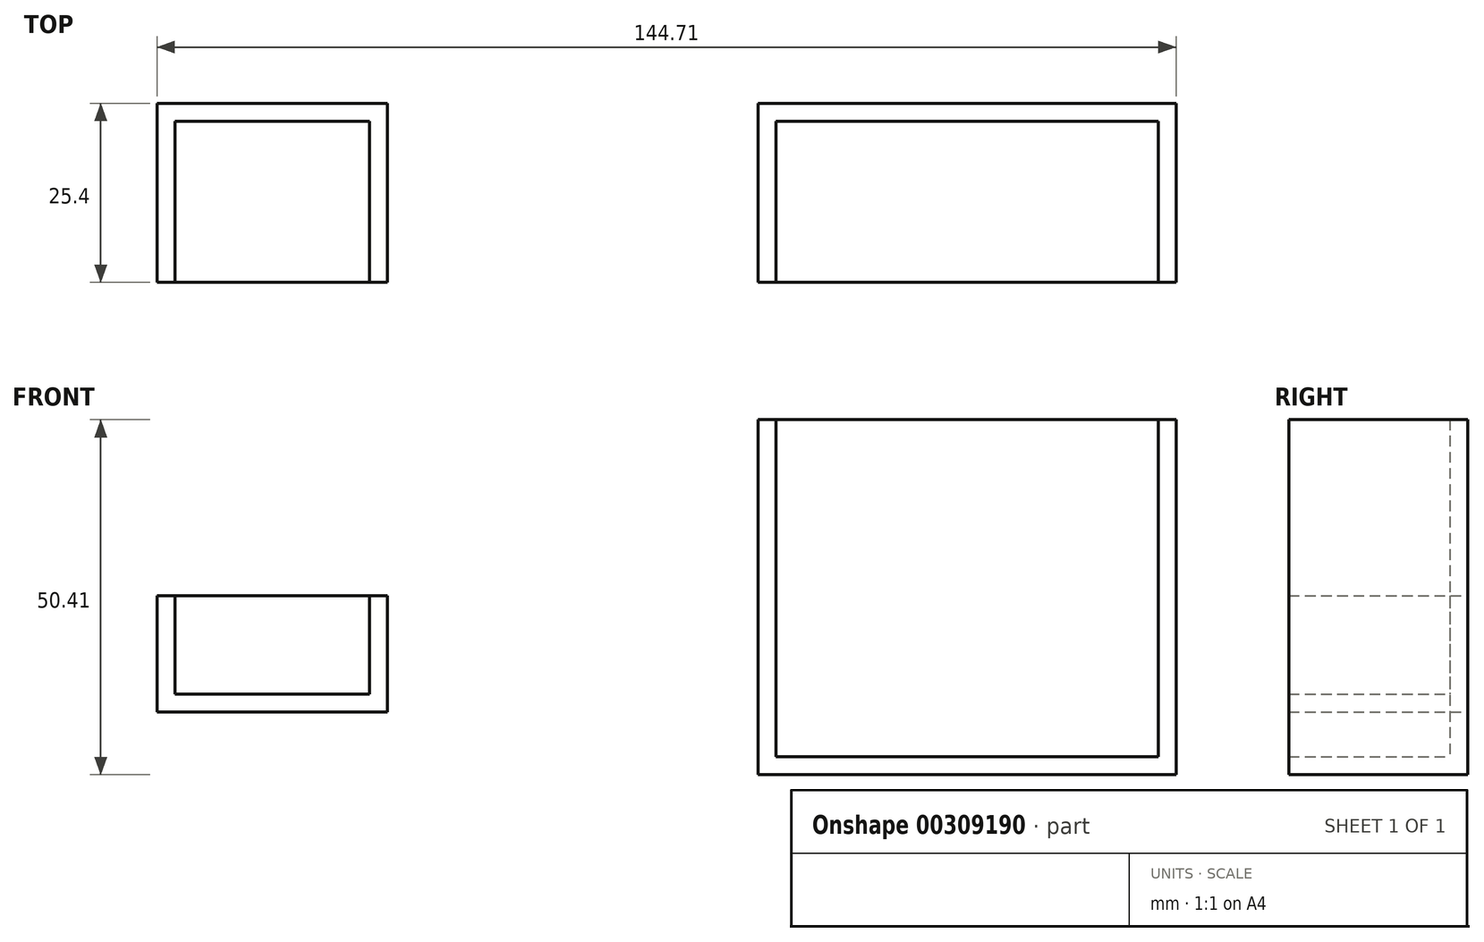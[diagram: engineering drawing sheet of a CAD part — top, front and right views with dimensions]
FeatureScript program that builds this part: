
annotation { "Feature Type Name" : "Feature", "Feature Type Description" : "" }
export const myFeature = defineFeature(function(context is Context, id is Id, definition is map)
    precondition{}
    {
        {
            var Q0;
            Q0=qCreatedBy(makeId("Front.planeOp"),FACE);
            var sketch = newSketch(context, id + "F0", { "sketchPlane" : qUnion([Q0])});
            skLineSegment(sketch, "E0.bottom", {"start": v(-111.29, 57.65) * mm, "end": v(-78.58, 57.65) * mm});
            skLineSegment(sketch, "E0.top", {"start": v(-111.29, 41.14) * mm, "end": v(-78.58, 41.14) * mm});
            skLineSegment(sketch, "E0.left", {"start": v(-111.29, 57.65) * mm, "end": v(-111.29, 41.14) * mm});
            skLineSegment(sketch, "E0.right", {"start": v(-78.58, 57.65) * mm, "end": v(-78.58, 41.14) * mm});
            skLineSegment(sketch, "E1.bottom", {"start": v(-25.96, 82.64) * mm, "end": v(33.42, 82.64) * mm});
            skLineSegment(sketch, "E1.top", {"start": v(-25.96, 32.23) * mm, "end": v(33.42, 32.23) * mm});
            skLineSegment(sketch, "E1.left", {"start": v(-25.96, 82.64) * mm, "end": v(-25.96, 32.23) * mm});
            skLineSegment(sketch, "E1.right", {"start": v(33.42, 82.64) * mm, "end": v(33.42, 32.23) * mm});
            skSolve(sketch);
        }
        {
            var Q0;
            Q0 = qSketchRegion(id + "F0", true);
            extrude(context, id + "F1", {"entities" : qUnion([Q0]), "depth" : 25.4 * mm});
        }
        {
            var Q0;
            Q0=makeQuery(id+"F1.opExtrude","SWEPT_FACE",FACE,{"disambiguationData":[OSD([sQuery(id+"F0.wireOp",EDGE,"E0.bottom")])]});
            var Q1;
            Q1=makeQuery(id+"F1.opExtrude","CAP_FACE",FACE,{"disambiguationData":[OSD([sQuery(id+"F0.wireOp",EDGE,"E0.bottom"),sQuery(id+"F0.wireOp",EDGE,"E0.top"),sQuery(id+"F0.wireOp",EDGE,"E0.left"),sQuery(id+"F0.wireOp",EDGE,"E0.right")])],"isStart":false});
            var Q2;
            Q2=makeQuery(id+"F1.opExtrude","CAP_FACE",FACE,{"disambiguationData":[OSD([sQuery(id+"F0.wireOp",EDGE,"E1.bottom"),sQuery(id+"F0.wireOp",EDGE,"E1.top"),sQuery(id+"F0.wireOp",EDGE,"E1.left"),sQuery(id+"F0.wireOp",EDGE,"E1.right")])],"isStart":false});
            var Q3;
            Q3=makeQuery(id+"F1.opExtrude","SWEPT_FACE",FACE,{"disambiguationData":[OSD([sQuery(id+"F0.wireOp",EDGE,"E1.bottom")])]});
            shell(context, id + "F2", {"entities" : qUnion([Q0, Q1, Q2, Q3]), "thickness" : 2.54 * mm});
        }
    });
